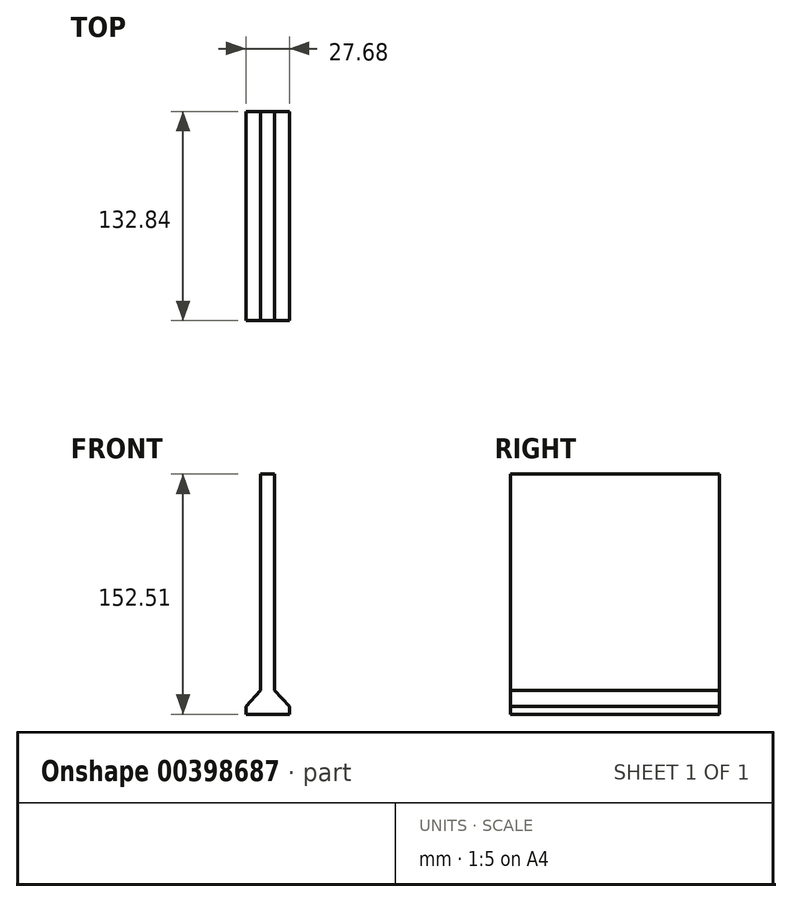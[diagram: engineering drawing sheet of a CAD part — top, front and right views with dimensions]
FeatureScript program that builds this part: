
annotation { "Feature Type Name" : "Feature", "Feature Type Description" : "" }
export const myFeature = defineFeature(function(context is Context, id is Id, definition is map)
    precondition{}
    {
        {
            var Q0;
            Q0=qCreatedBy(makeId("Front.planeOp"),FACE);
            var sketch = newSketch(context, id + "F0", { "sketchPlane" : qUnion([Q0])});
            skLineSegment(sketch, "E0", {"start": v(-4.48, 76.19) * mm, "end": v(-4.48, -61.13) * mm});
            skLineSegment(sketch, "E1", {"start": v(-4.48, -61.13) * mm, "end": v(-13.84, -71.31) * mm});
            skLineSegment(sketch, "E2", {"start": v(-13.84, -71.31) * mm, "end": v(-13.84, -76.32) * mm});
            skLineSegment(sketch, "E3", {"start": v(-13.84, -76.32) * mm, "end": v(0, -76.32) * mm});
            skLineSegment(sketch, "E4", {"start": v(-4.48, 76.19) * mm, "end": v(0, 76.19) * mm});
            skLineSegment(sketch, "E5.MirrorCS", {"start": v(4.48, 76.19) * mm, "end": v(4.48, -61.13) * mm});
            skLineSegment(sketch, "E6.MirrorCS", {"start": v(4.48, -61.13) * mm, "end": v(13.84, -71.31) * mm});
            skLineSegment(sketch, "E7.MirrorCS", {"start": v(13.84, -71.31) * mm, "end": v(13.84, -76.32) * mm});
            skLineSegment(sketch, "E8.MirrorCS", {"start": v(13.84, -76.32) * mm, "end": v(0, -76.32) * mm});
            skLineSegment(sketch, "E9.MirrorCS", {"start": v(4.48, 76.19) * mm, "end": v(0, 76.19) * mm});
            skSolve(sketch);
        }
        {
            var Q0;
            Q0 = qSketchRegion(id + "F0", true);
            extrude(context, id + "F1", {"entities" : qUnion([Q0]), "depth" : 132.84 * mm});
        }
    });
